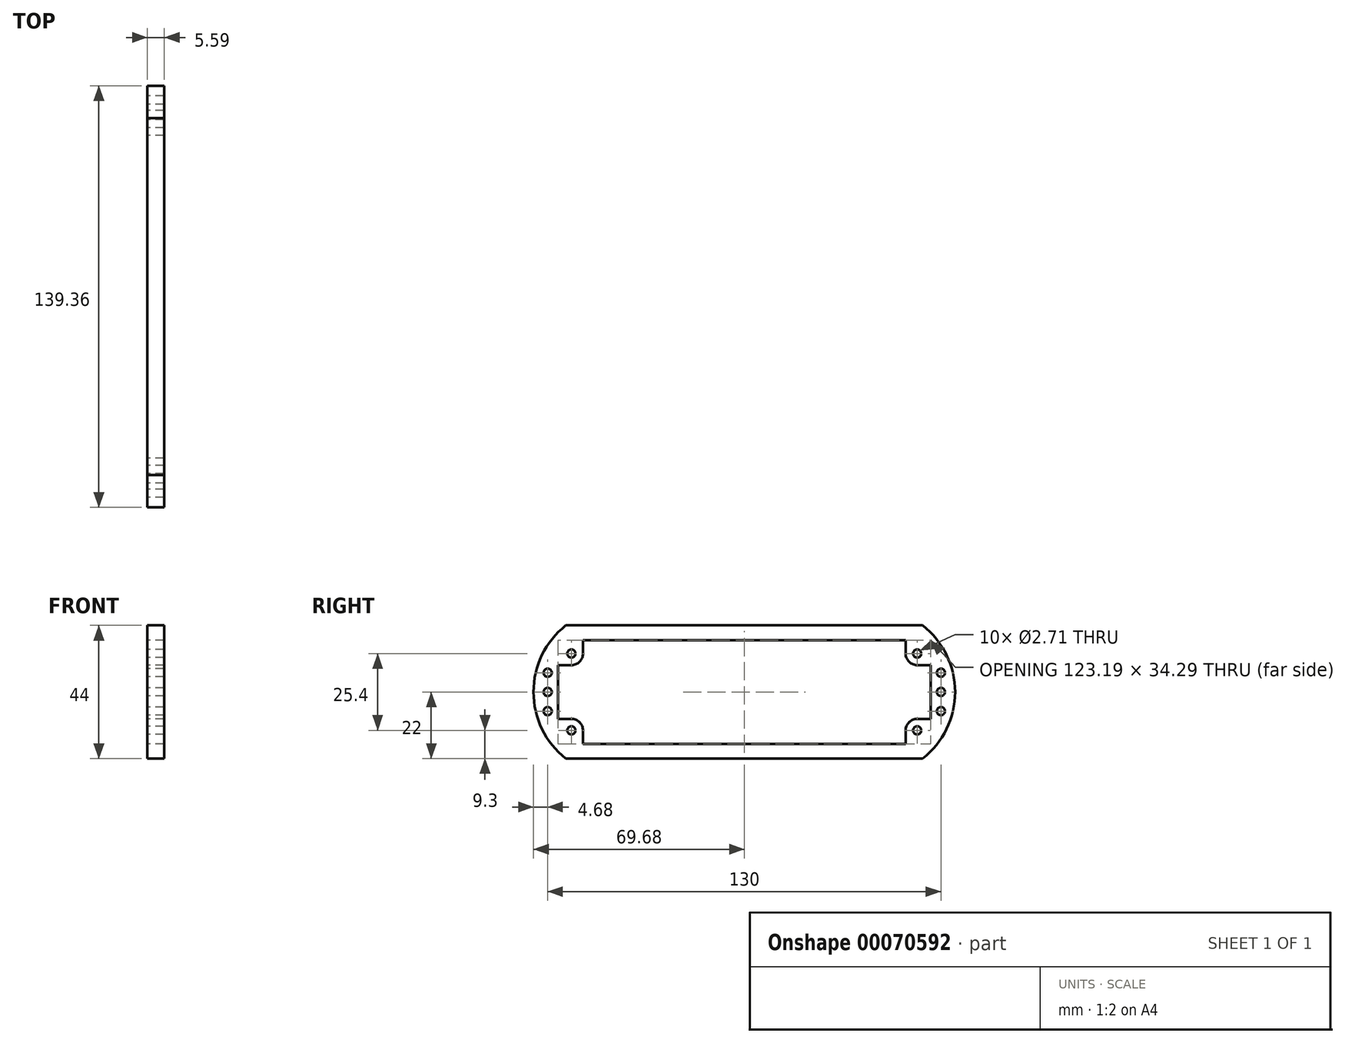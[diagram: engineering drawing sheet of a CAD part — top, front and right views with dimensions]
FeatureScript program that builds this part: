
annotation { "Feature Type Name" : "Feature", "Feature Type Description" : "" }
export const myFeature = defineFeature(function(context is Context, id is Id, definition is map)
    precondition{}
    {
        {
            var Q0;
            Q0=qCreatedBy(makeId("Right.planeOp"),FACE);
            var sketch = newSketch(context, id + "F0", { "sketchPlane" : qUnion([Q0])});
            skLineSegment(sketch, "E0.rect.bottom", {"start": v(59, 22) * mm, "end": v(-59, 22) * mm});
            skLineSegment(sketch, "E0.rect.top", {"start": v(59, -22) * mm, "end": v(-59, -22) * mm});
            skLineSegment(sketch, "E0.rect.left", {"start": v(59, 22) * mm, "end": v(59, -22) * mm, "construction": true});
            skLineSegment(sketch, "E0.rect.right", {"start": v(-59, 22) * mm, "end": v(-59, -22) * mm, "construction": true});
            skPoint(sketch, "E0.rect.middle", {"position": v(0, 0) * mm});
            skLineSegment(sketch, "E1", {"start": v(-59, 0) * mm, "end": v(59, 0) * mm, "construction": true});
            skArc(sketch, "E2", {"start": v(-59, 22) * mm, "mid": v(-69.68, 0) * mm, "end": v(-59, -22) * mm});
            skArc(sketch, "E3", {"start": v(59, -22) * mm, "mid": v(69.68, 0) * mm, "end": v(59, 22) * mm});
            skLineSegment(sketch, "E4.0", {"start": v(53.34, 17.14) * mm, "end": v(-53.34, 17.15) * mm});
            skLineSegment(sketch, "E4.2", {"start": v(53.34, -17.15) * mm, "end": v(-53.34, -17.14) * mm});
            skLineSegment(sketch, "E5.0", {"start": v(-53.34, 17.15) * mm, "end": v(-53.34, 12.7) * mm});
            skLineSegment(sketch, "E6.0", {"start": v(53.34, 17.15) * mm, "end": v(53.34, 12.7) * mm});
            skCircle(sketch, "E7", {"center": v(-65, 0) * mm, "radius": 1.35 * mm});
            skCircle(sketch, "E8", {"center": v(65, 0) * mm, "radius": 1.35 * mm});
            skCircle(sketch, "E9", {"center": v(-57.15, 12.7) * mm, "radius": 1.35 * mm});
            skCircle(sketch, "E10", {"center": v(-57.15, -12.7) * mm, "radius": 1.35 * mm});
            skCircle(sketch, "E11", {"center": v(57.15, -12.7) * mm, "radius": 1.35 * mm});
            skCircle(sketch, "E12", {"center": v(57.15, 12.7) * mm, "radius": 1.35 * mm});
            skLineSegment(sketch, "E13", {"start": v(-57.15, 12.7) * mm, "end": v(57.15, -12.7) * mm, "construction": true});
            skLineSegment(sketch, "E14", {"start": v(-53.34, 17.14) * mm, "end": v(53.34, -17.15) * mm, "construction": true});
            skLineSegment(sketch, "E15.bottom", {"start": v(61.6, 8.9) * mm, "end": v(57.15, 8.9) * mm});
            skLineSegment(sketch, "E15.top", {"start": v(61.6, -8.9) * mm, "end": v(57.15, -8.9) * mm});
            skLineSegment(sketch, "E15.left", {"start": v(61.6, 8.9) * mm, "end": v(61.6, -8.9) * mm});
            skLineSegment(sketch, "E15.right", {"start": v(-61.6, 8.9) * mm, "end": v(-61.6, -8.9) * mm});
            skLineSegment(sketch, "E16", {"start": v(-61.6, 8.89) * mm, "end": v(61.6, -8.9) * mm, "construction": true});
            skLineSegment(sketch, "E17.trimOffspring", {"start": v(-57.15, 8.9) * mm, "end": v(-61.6, 8.9) * mm});
            skLineSegment(sketch, "E18.trimOffspring", {"start": v(-57.15, -8.9) * mm, "end": v(-61.6, -8.9) * mm});
            skLineSegment(sketch, "E19.trimOffspring", {"start": v(53.34, -12.7) * mm, "end": v(53.34, -17.14) * mm});
            skLineSegment(sketch, "E20.trimOffspring", {"start": v(-53.34, -12.7) * mm, "end": v(-53.34, -17.15) * mm});
            skPoint(sketch, "E21.visualSharp", {"position": v(53.34, 8.9) * mm});
            skArc(sketch, "E21.filletArc", {"start": v(53.34, 12.7) * mm, "mid": v(54.46, 10) * mm, "end": v(57.15, 8.9) * mm});
            skPoint(sketch, "E22.visualSharp", {"position": v(53.34, -8.9) * mm});
            skArc(sketch, "E22.filletArc", {"start": v(57.15, -8.9) * mm, "mid": v(54.46, -10) * mm, "end": v(53.34, -12.7) * mm});
            skPoint(sketch, "E23.visualSharp", {"position": v(-53.34, -8.9) * mm});
            skArc(sketch, "E23.filletArc", {"start": v(-53.34, -12.7) * mm, "mid": v(-54.46, -10) * mm, "end": v(-57.15, -8.9) * mm});
            skPoint(sketch, "E24.visualSharp", {"position": v(-53.34, 8.9) * mm});
            skArc(sketch, "E24.filletArc", {"start": v(-57.15, 8.9) * mm, "mid": v(-54.46, 10) * mm, "end": v(-53.34, 12.7) * mm});
            skCircle(sketch, "E25", {"center": v(-65, 6.35) * mm, "radius": 1.35 * mm});
            skCircle(sketch, "E26", {"center": v(-65, -6.35) * mm, "radius": 1.35 * mm});
            skCircle(sketch, "E27", {"center": v(65, 6.35) * mm, "radius": 1.35 * mm});
            skCircle(sketch, "E28", {"center": v(65, -6.35) * mm, "radius": 1.35 * mm});
            skLineSegment(sketch, "E29", {"start": v(-65, 6.35) * mm, "end": v(-65, -6.35) * mm, "construction": true});
            skSolve(sketch);
        }
        {
            var Q0;
            Q0=makeQuery(id+"F0.imprint","IMPRINT",FACE,{"disambiguationData":[TD([[makeQuery(id+"F0.imprint","IMPRINT",EDGE,{"derivedFrom":sQuery(id+"F0.wireOp",EDGE,"E0.rect.bottom")}),1.0]])]});
            extrude(context, id + "F1", {"entities" : qUnion([Q0]), "depth" : 5.6 * mm});
        }
    });
